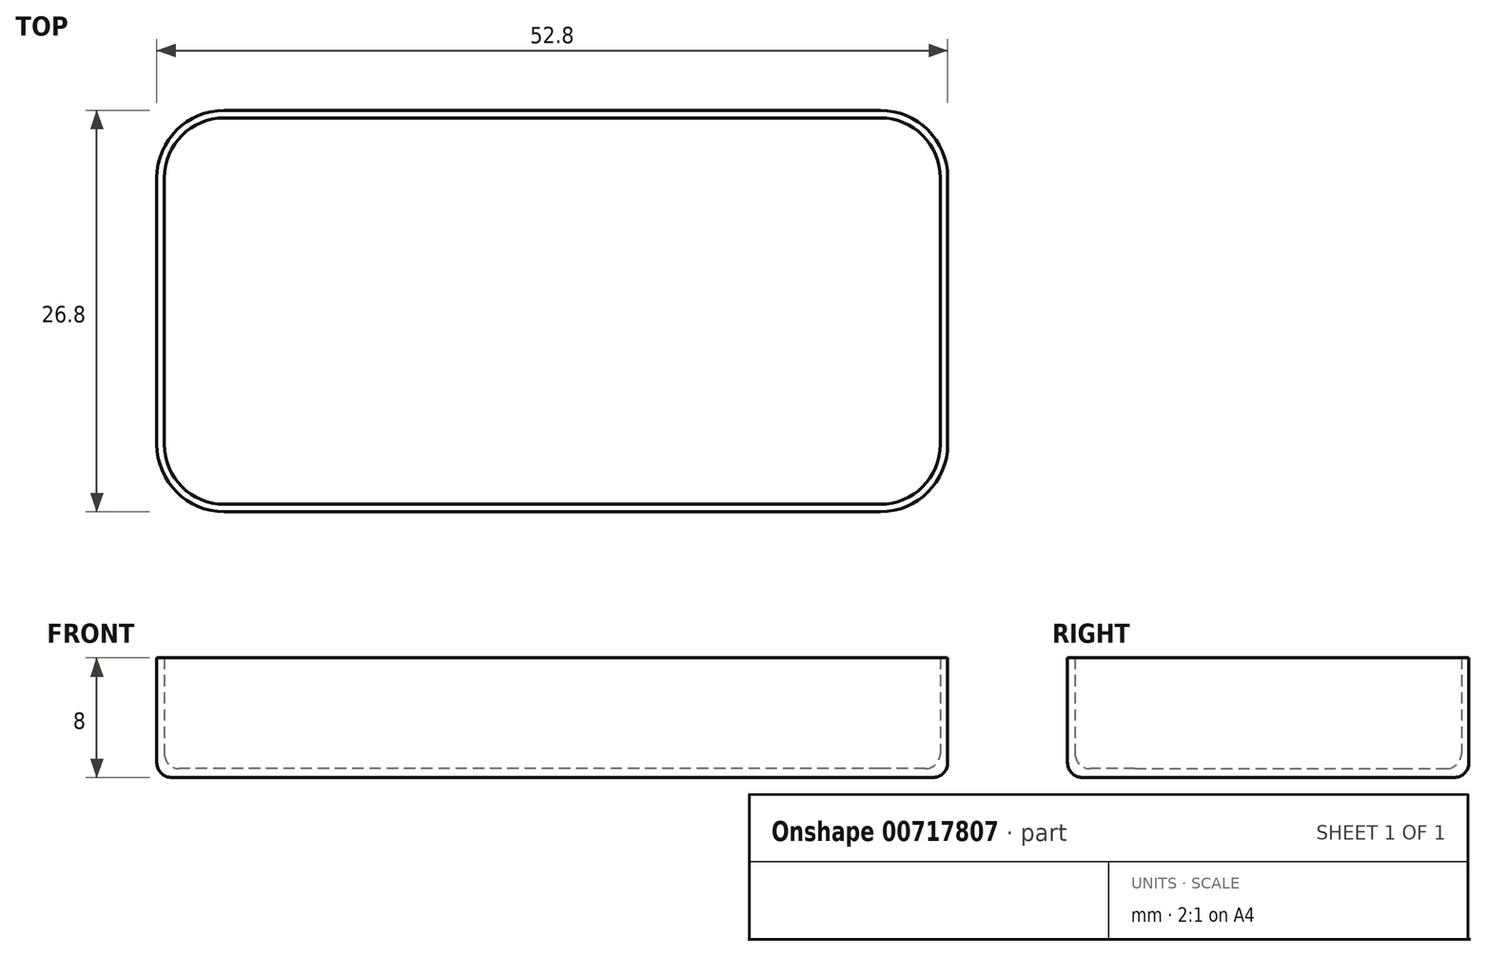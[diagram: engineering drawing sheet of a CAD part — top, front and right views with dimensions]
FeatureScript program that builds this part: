
annotation { "Feature Type Name" : "Feature", "Feature Type Description" : "" }
export const myFeature = defineFeature(function(context is Context, id is Id, definition is map)
    precondition{}
    {
        {
            var Q0;
            Q0=qCreatedBy(makeId("Top.planeOp"),FACE);
            var sketch = newSketch(context, id + "F0", { "sketchPlane" : qUnion([Q0])});
            skLineSegment(sketch, "E0.bottom", {"start": v(26.4, -13.4) * mm, "end": v(-26.4, -13.4) * mm});
            skLineSegment(sketch, "E0.top", {"start": v(26.4, 13.4) * mm, "end": v(-26.4, 13.4) * mm});
            skLineSegment(sketch, "E0.left", {"start": v(26.4, -13.4) * mm, "end": v(26.4, 13.4) * mm});
            skLineSegment(sketch, "E0.right", {"start": v(-26.4, -13.4) * mm, "end": v(-26.4, 13.4) * mm});
            skPoint(sketch, "E0.middle", {"position": v(0, 0) * mm});
            skLineSegment(sketch, "E1.bottom", {"start": v(-25.9, 12.9) * mm, "end": v(25.9, 12.9) * mm});
            skLineSegment(sketch, "E1.top", {"start": v(-25.9, -12.9) * mm, "end": v(25.9, -12.9) * mm});
            skLineSegment(sketch, "E1.left", {"start": v(-25.9, 12.9) * mm, "end": v(-25.9, -12.9) * mm});
            skLineSegment(sketch, "E1.right", {"start": v(25.9, 12.9) * mm, "end": v(25.9, -12.9) * mm});
            skSolve(sketch);
        }
        {
            var Q0;
            Q0=qSketchRegion(id+"F0",true);
            var Q1;
            Q1=makeQuery(id+"F0.imprint","IMPRINT",FACE,{"disambiguationData":[TD([[makeQuery(id+"F0.imprint","IMPRINT",EDGE,{"derivedFrom":sQuery(id+"F0.wireOp",EDGE,"E1.bottom")}),-1.0]])]});
            extrude(context, id + "F1", {"entities" : qUnion([Q0, Q1]), "depth" : .6 * mm, "offsetDistance" : 25 * mm});
        }
        {
            var Q0;
            Q0=makeQuery(id+"F0.imprint","IMPRINT",FACE,{"disambiguationData":[TD([[makeQuery(id+"F0.imprint","IMPRINT",EDGE,{"derivedFrom":sQuery(id+"F0.wireOp",EDGE,"E0.bottom")}),-1.0]])]});
            extrude(context, id + "F2", {"entities" : qUnion([Q0]), "operationType" : NewBodyOperationType.ADD, "depth" : 8 * mm, "offsetDistance" : 25 * mm});
        }
        {
            var Q0;
            Q0=makeQuery(id+"F2.opExtrude","SWEPT_EDGE",EDGE,{"disambiguationData":[OSD([sQuery(id+"F0.wireOp",EDGE,"E1.bottom"),sQuery(id+"F0.wireOp",EDGE,"E1.left")])]});
            var Q1;
            Q1=makeQuery(id+"F2.opExtrude","SWEPT_EDGE",EDGE,{"disambiguationData":[OSD([sQuery(id+"F0.wireOp",EDGE,"E1.bottom"),sQuery(id+"F0.wireOp",EDGE,"E1.right")])]});
            var Q2;
            Q2=makeQuery(id+"F2.opExtrude","SWEPT_EDGE",EDGE,{"disambiguationData":[OSD([sQuery(id+"F0.wireOp",EDGE,"E1.top"),sQuery(id+"F0.wireOp",EDGE,"E1.right")])]});
            var Q3;
            Q3=makeQuery(id+"F2.opExtrude","SWEPT_EDGE",EDGE,{"disambiguationData":[OSD([sQuery(id+"F0.wireOp",EDGE,"E1.top"),sQuery(id+"F0.wireOp",EDGE,"E1.left")])]});
            fillet(context, id + "F3", {"entities" : qUnion([Q0, Q1, Q2, Q3]), "radius" : 4 * mm, "tangentPropagation" : true, "allowEdgeOverflow" : false});
        }
        {
            var Q0;
            {var subQ0=sQuery(id+"F0.wireOp",EDGE,"E0.left");var subQ1=sQuery(id+"F0.wireOp",EDGE,"E0.top");Q0=makeQuery(id+"F2.boolean.opBoolean","MERGE",EDGE,{"derivedFrom":[makeQuery(id+"F1.opExtrude","SWEPT_EDGE",EDGE,{"disambiguationData":[OSD([subQ1,subQ0])]}),makeQuery(id+"F2.opExtrude","SWEPT_EDGE",EDGE,{"disambiguationData":[OSD([subQ1,subQ0])]})]});}
            var Q1;
            {var subQ0=sQuery(id+"F0.wireOp",EDGE,"E0.left");var subQ1=sQuery(id+"F0.wireOp",EDGE,"E0.bottom");Q1=makeQuery(id+"F2.boolean.opBoolean","MERGE",EDGE,{"derivedFrom":[makeQuery(id+"F1.opExtrude","SWEPT_EDGE",EDGE,{"disambiguationData":[OSD([subQ1,subQ0])]}),makeQuery(id+"F2.opExtrude","SWEPT_EDGE",EDGE,{"disambiguationData":[OSD([subQ1,subQ0])]})]});}
            var Q2;
            {var subQ0=sQuery(id+"F0.wireOp",EDGE,"E0.right");var subQ1=sQuery(id+"F0.wireOp",EDGE,"E0.top");Q2=makeQuery(id+"F2.boolean.opBoolean","MERGE",EDGE,{"derivedFrom":[makeQuery(id+"F1.opExtrude","SWEPT_EDGE",EDGE,{"disambiguationData":[OSD([subQ1,subQ0])]}),makeQuery(id+"F2.opExtrude","SWEPT_EDGE",EDGE,{"disambiguationData":[OSD([subQ1,subQ0])]})]});}
            var Q3;
            {var subQ0=sQuery(id+"F0.wireOp",EDGE,"E0.right");var subQ1=sQuery(id+"F0.wireOp",EDGE,"E0.bottom");Q3=makeQuery(id+"F2.boolean.opBoolean","MERGE",EDGE,{"derivedFrom":[makeQuery(id+"F1.opExtrude","SWEPT_EDGE",EDGE,{"disambiguationData":[OSD([subQ1,subQ0])]}),makeQuery(id+"F2.opExtrude","SWEPT_EDGE",EDGE,{"disambiguationData":[OSD([subQ1,subQ0])]})]});}
            fillet(context, id + "F4", {"entities" : qUnion([Q0, Q1, Q2, Q3]), "radius" : 4.5 * mm, "tangentPropagation" : true, "allowEdgeOverflow" : false});
        }
        {
            var Q0;
            Q0=makeQuery(id+"F2.boolean.opBoolean","INTERSECT",EDGE,{"derivedFrom":[makeQuery(id+"F1.opExtrude","CAP_FACE",FACE,{"disambiguationData":[OSD([sQuery(id+"F0.wireOp",EDGE,"E0.bottom"),sQuery(id+"F0.wireOp",EDGE,"E0.top"),sQuery(id+"F0.wireOp",EDGE,"E0.left"),sQuery(id+"F0.wireOp",EDGE,"E0.right")])],"isStart":false}),makeQuery(id+"F2.opExtrude","SWEPT_FACE",FACE,{"disambiguationData":[OSD([sQuery(id+"F0.wireOp",EDGE,"E1.bottom")])]})]});
            var Q1;
            Q1=makeQuery(id+"F1.opExtrude","CAP_EDGE",EDGE,{"disambiguationData":[OSD([sQuery(id+"F0.wireOp",EDGE,"E0.top")])],"isStart":true});
            fillet(context, id + "F5", {"entities" : qUnion([Q0, Q1]), "radius" : 1 * mm, "tangentPropagation" : true, "allowEdgeOverflow" : false});
        }
    });
